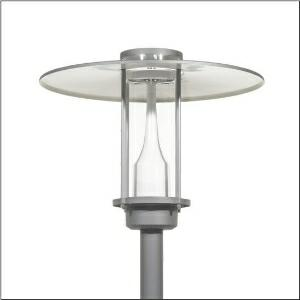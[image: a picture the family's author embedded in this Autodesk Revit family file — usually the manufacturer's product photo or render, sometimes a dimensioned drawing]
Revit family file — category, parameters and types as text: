
# Revit family: city-light_plus_iq___p1_0a_5xa5275nf14hp_e05b
name_source: partatom
category: Lighting Fixtures
units: mm (PartAtom-declared; Revit-internal decimal feet)

## family parameters
Cut with Voids When Loaded = No
Host = Face
Light Source = No
Part Type = Normal
Room Calculation Point = No
Round Connector Dimension = Use Diameter
Shared = No

## types (1)
- --- (1 x LED, 4020 lm, 33.6 W, 2700K)
    Apparent Load = 34 VA
    CIE Flux Codes = 30 60 90 96 100
    Color Rendering = 70
    Color Temperature = 2700K
    Default Elevation = 1800 mm
    Description = City-Light Plus iQ, mast luminaire, Module 540 iQ-SR, primary light control with 3 zone facetted reflector, of plastic, silver coated, highly specular, structured, primary optical cover: cover, of PMMA, transparent, light distribution: P1.0a, light emission: direct distribution, primary light characteristic: strongly asymmetric, installation type: post-top, LED, High Power LED, rated luminous flux: 4.020lm, luminous efficacy: 120lm/W, light colour: 727, colour temperature: 2700K, control gear: iQ Street-Remote, control: pre-setting: logarithmic dimming characteristic, Street-Remote, Auto-Match, Temp-Guard, Lumen-Switch, Night-Set, Smart-Wire, Light-Fading, Desk-Remote (wireless, voltage-free reading and setting of iQ features in the workshop via application-optimized NFC function/RFID function), optimised constant luminous flux control (CLO 2.0), with terminal, 6-pole, max. 2.5mm², mains connection: 230..240V, AC, 50/60Hz, start of lifetime: 34W, end of service life: 36W, reduction: 15W, luminaire housing, upper part, of glass-fibre reinforced polyester, coated, Siteco® metallic grey (DB 702S), diameter: 750mm, height: 590mm, spigot size: d x l = 76 x 70mm (post-top) | with reducer (optional accessory) 60 x 70mm, mounting height: 3..5m, post-top mast mounting element, of diecast aluminium, coated, Siteco® metallic grey (DB 702S), Module 540 iQ-SR, traffic white (RAL 9016), equipment: Power, protection rating (complete): IP65, insulation class (complete): insulation class II (safety insulation), certification: CE, ENEC, VDE, packaging unit: 1 piece

Light Distribution: P1.0a
    Height = 590 mm
    Lamp = 1 x LED
    Lamp Light Flux = 4020 lm
    Lamp Power = 33.6 W
    Lamp count = 1
    Length = 750 mm
    Luminous efficacy = 120 lm/W
    Manufacturer = Siteco
    ModVariant = No
    Model = 5XA5275NF14HP
    Number of Poles = 1
    OnlyDefault = Yes
    Power Factor = 1
    Product Name = City-Light Plus iQ | P1.0a
    Product group = mast luminaire | pylon top
    ProductGroupID = 6100
    Protection Class = Protection class II
    Protection Degree = IP 65
    RLX_Detail_Level = 1
    RLX_Emergency_Light_Flux = 0 lm
    RLX_Emergency_Type = 0
    RLX_Emergency_Type_DB = No
    RlxData = <blob elided: 35049 chars, md5=fea79c83>
    Socket = socket
    Standby Power = 0 W
    System Light Flux = 4020 lm
    System Power = 34 W
    Type Comments = factory setting: luminous flux: 100 % | dim-lin: 254 | 695 mA
    Type Image = l_1006456.jpg
    URL = http://relux.com
    VarID = @adj_152846
    Voltage = 0 V
    Weight = 0.00 kg
    Width = 0 mm  [stored 0 ft]

note: [stored X ft] marks values corroborated as IEEE doubles in the binary element streams (Revit-internal decimal feet)

## geometry (parser evidence)
native form markers: Blend x4, Sweep x9
no freeform markers — native parametric forms only
